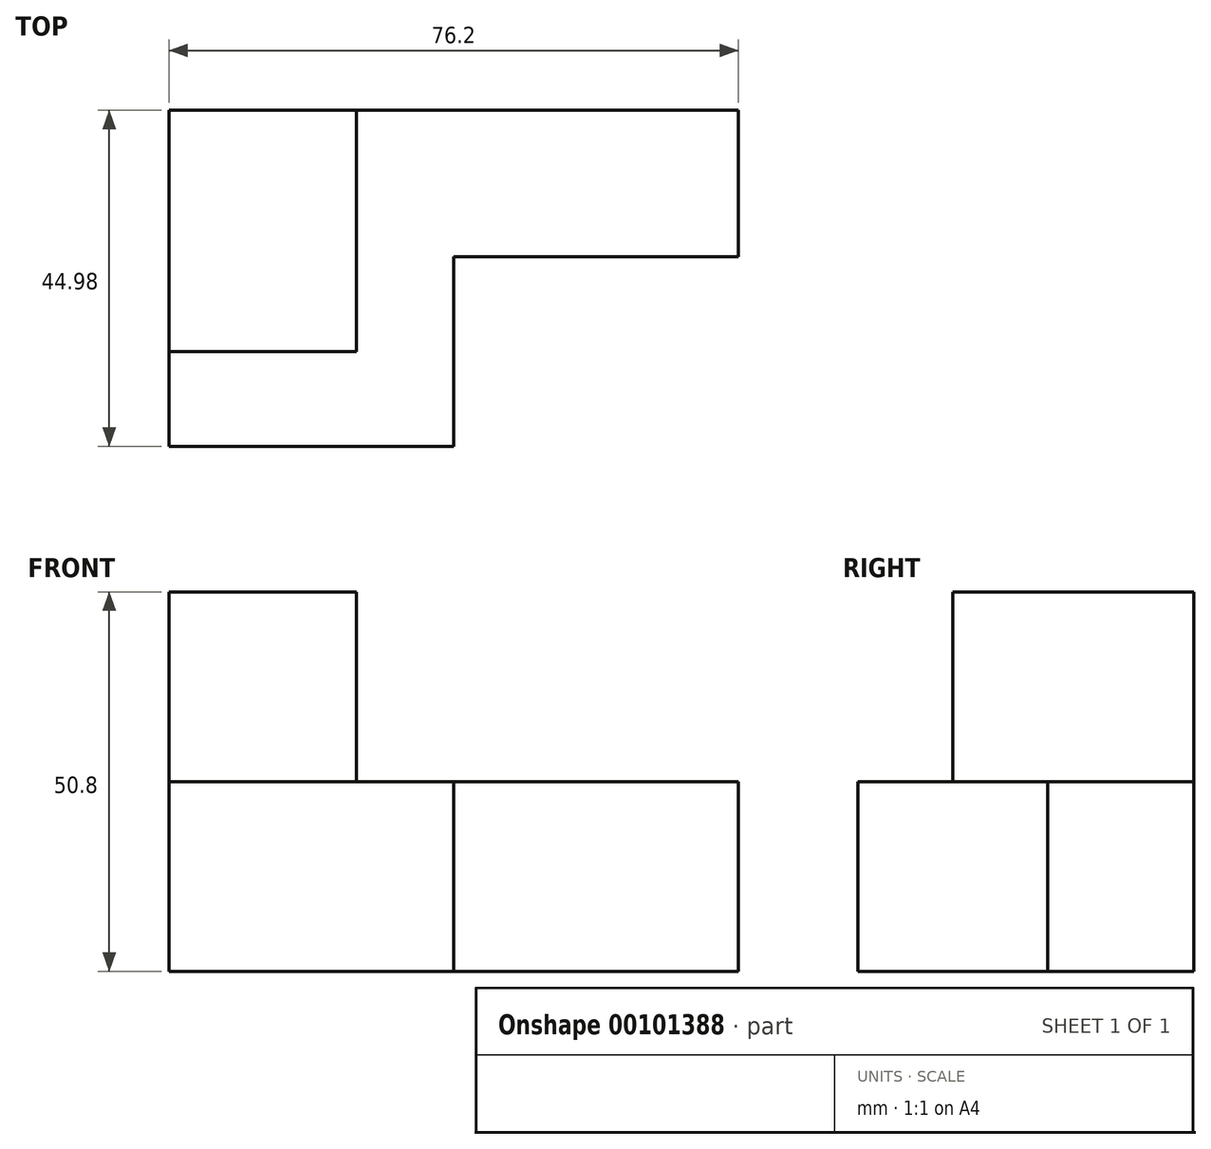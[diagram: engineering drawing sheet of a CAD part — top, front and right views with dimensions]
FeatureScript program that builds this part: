
annotation { "Feature Type Name" : "Feature", "Feature Type Description" : "" }
export const myFeature = defineFeature(function(context is Context, id is Id, definition is map)
    precondition{}
    {
        {
            var Q0;
            Q0=qCreatedBy(makeId("Front.planeOp"),FACE);
            var sketch = newSketch(context, id + "F0", { "sketchPlane" : qUnion([Q0])});
            skLineSegment(sketch, "E0", {"start": v(0, 0) * mm, "end": v(0, 50.8) * mm});
            skLineSegment(sketch, "E1", {"start": v(0, 50.8) * mm, "end": v(25.08, 50.8) * mm});
            skLineSegment(sketch, "E2", {"start": v(25.08, 50.8) * mm, "end": v(25.08, 25.4) * mm});
            skLineSegment(sketch, "E3", {"start": v(25.08, 25.4) * mm, "end": v(76.2, 25.4) * mm});
            skLineSegment(sketch, "E4", {"start": v(76.2, 25.4) * mm, "end": v(76.2, 0) * mm});
            skLineSegment(sketch, "E5", {"start": v(76.2, 0) * mm, "end": v(0, 0) * mm});
            skLineSegment(sketch, "E6", {"start": v(0, 25.4) * mm, "end": v(25.08, 25.4) * mm});
            skLineSegment(sketch, "E7", {"start": v(38.1, 25.4) * mm, "end": v(38.1, 0) * mm});
            skPoint(sketch, "E7.endSnap0", {"position": v(38.1, 0) * mm});
            skSolve(sketch);
        }
        {
            var Q0;
            Q0=qCreatedBy(makeId("Right.planeOp"),FACE);
            var sketch = newSketch(context, id + "F1", { "sketchPlane" : qUnion([Q0])});
            skLineSegment(sketch, "E8", {"start": v(0, 25.4) * mm, "end": v(12.7, 25.4) * mm});
            skLineSegment(sketch, "E9", {"start": v(12.7, 25.4) * mm, "end": v(12.7, 50.8) * mm});
            skLineSegment(sketch, "E10", {"start": v(12.7, 50.8) * mm, "end": v(0, 50.8) * mm});
            skLineSegment(sketch, "E11", {"start": v(0, 50.8) * mm, "end": v(0, 25.4) * mm});
            skSolve(sketch);
        }
        {
            var Q0;
            Q0=qCreatedBy(makeId("Top.planeOp"),FACE);
            var sketch = newSketch(context, id + "F2", { "sketchPlane" : qUnion([Q0])});
            skLineSegment(sketch, "E12", {"start": v(76.2, 25.4) * mm, "end": v(38.1, 25.4) * mm});
            skLineSegment(sketch, "E13", {"start": v(38.1, 25.4) * mm, "end": v(38.1, 0) * mm});
            skLineSegment(sketch, "E14", {"start": v(38.1, 0) * mm, "end": v(76.5, 0) * mm});
            skLineSegment(sketch, "E15", {"start": v(76.5, 0) * mm, "end": v(76.2, 25.4) * mm});
            skSolve(sketch);
        }
        {
            var Q0;
            Q0 = qSketchRegion(id + "F0", true);
            extrude(context, id + "F3", {"entities" : qUnion([Q0]), "oppositeDirection" : true, "depth" : 44.98 * mm});
        }
        {
            var Q0;
            Q0 = qSketchRegion(id + "F1", true);
            extrude(context, id + "F4", {"entities" : qUnion([Q0]), "operationType" : NewBodyOperationType.REMOVE, "depth" : 25.6 * mm});
        }
        {
            var Q0;
            Q0 = qSketchRegion(id + "F2", true);
            extrude(context, id + "F5", {"entities" : qUnion([Q0]), "operationType" : NewBodyOperationType.REMOVE, "depth" : 25.4 * mm});
        }
    });
